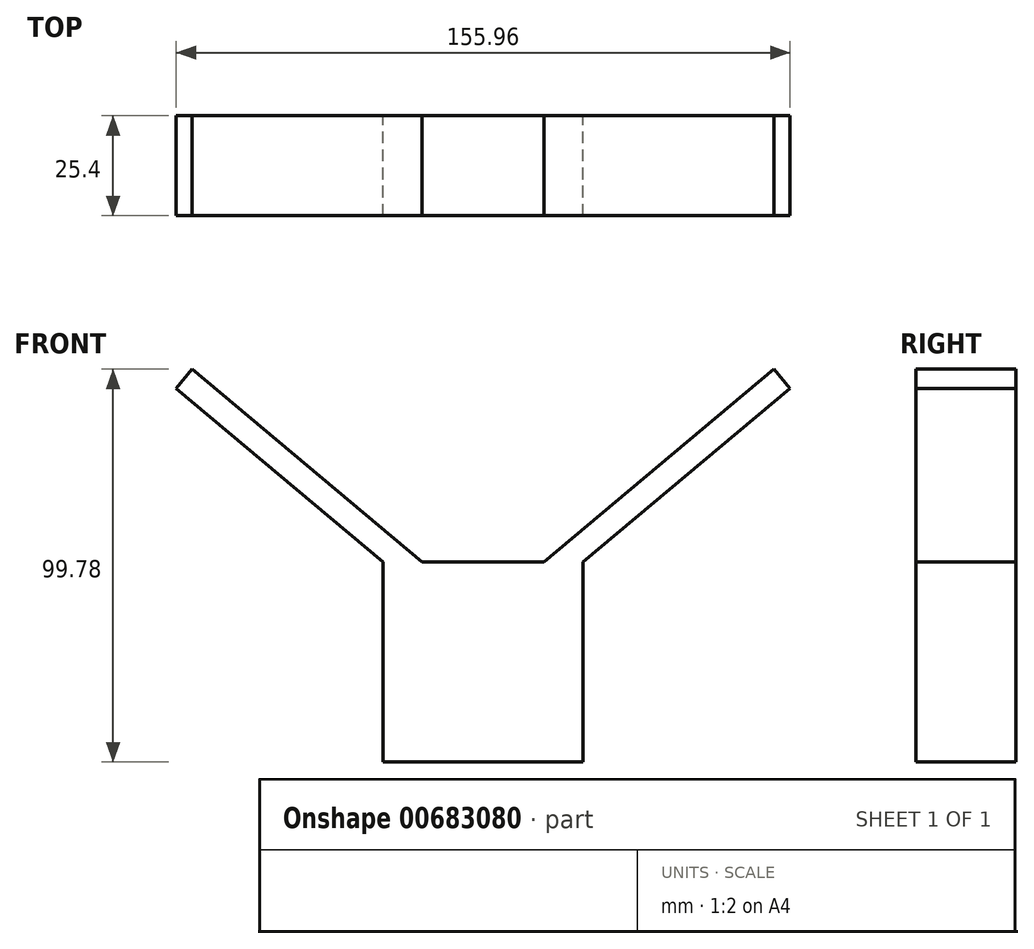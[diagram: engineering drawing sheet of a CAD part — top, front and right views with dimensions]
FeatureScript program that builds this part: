
annotation { "Feature Type Name" : "Feature", "Feature Type Description" : "" }
export const myFeature = defineFeature(function(context is Context, id is Id, definition is map)
    precondition{}
    {
        {
            var Q0;
            Q0=qCreatedBy(makeId("Front.planeOp"),FACE);
            var sketch = newSketch(context, id + "F0", { "sketchPlane" : qUnion([Q0])});
            skLineSegment(sketch, "E0.bottom", {"start": v(-15.52, 25.4) * mm, "end": v(15.52, 25.4) * mm});
            skLineSegment(sketch, "E0.top", {"start": v(-25.4, -25.4) * mm, "end": v(25.4, -25.4) * mm});
            skLineSegment(sketch, "E0.left", {"start": v(-25.4, 25.4) * mm, "end": v(-25.4, -25.4) * mm});
            skLineSegment(sketch, "E0.right", {"start": v(25.4, 25.4) * mm, "end": v(25.4, -25.4) * mm});
            skPoint(sketch, "E0.middle", {"position": v(0, 0) * mm});
            skLineSegment(sketch, "E1", {"start": v(-25.4, 25.4) * mm, "end": v(-77.98, 69.52) * mm});
            skLineSegment(sketch, "E2", {"start": v(-77.98, 69.52) * mm, "end": v(-73.9, 74.38) * mm});
            skLineSegment(sketch, "E3", {"start": v(-73.9, 74.38) * mm, "end": v(-15.52, 25.4) * mm});
            skLineSegment(sketch, "E4", {"start": v(25.4, 25.4) * mm, "end": v(77.98, 69.52) * mm});
            skLineSegment(sketch, "E5", {"start": v(77.98, 69.52) * mm, "end": v(73.9, 74.38) * mm});
            skLineSegment(sketch, "E6", {"start": v(73.9, 74.38) * mm, "end": v(15.52, 25.4) * mm});
            skLineSegment(sketch, "E7", {"start": v(0, 25.4) * mm, "end": v(0, 0) * mm, "construction": true});
            skSolve(sketch);
        }
        {
            var Q0;
            Q0 = qSketchRegion(id + "F0", true);
            extrude(context, id + "F1", {"entities" : qUnion([Q0]), "depth" : 25.4 * mm, "offsetDistance" : 25.4 * mm});
        }
    });
